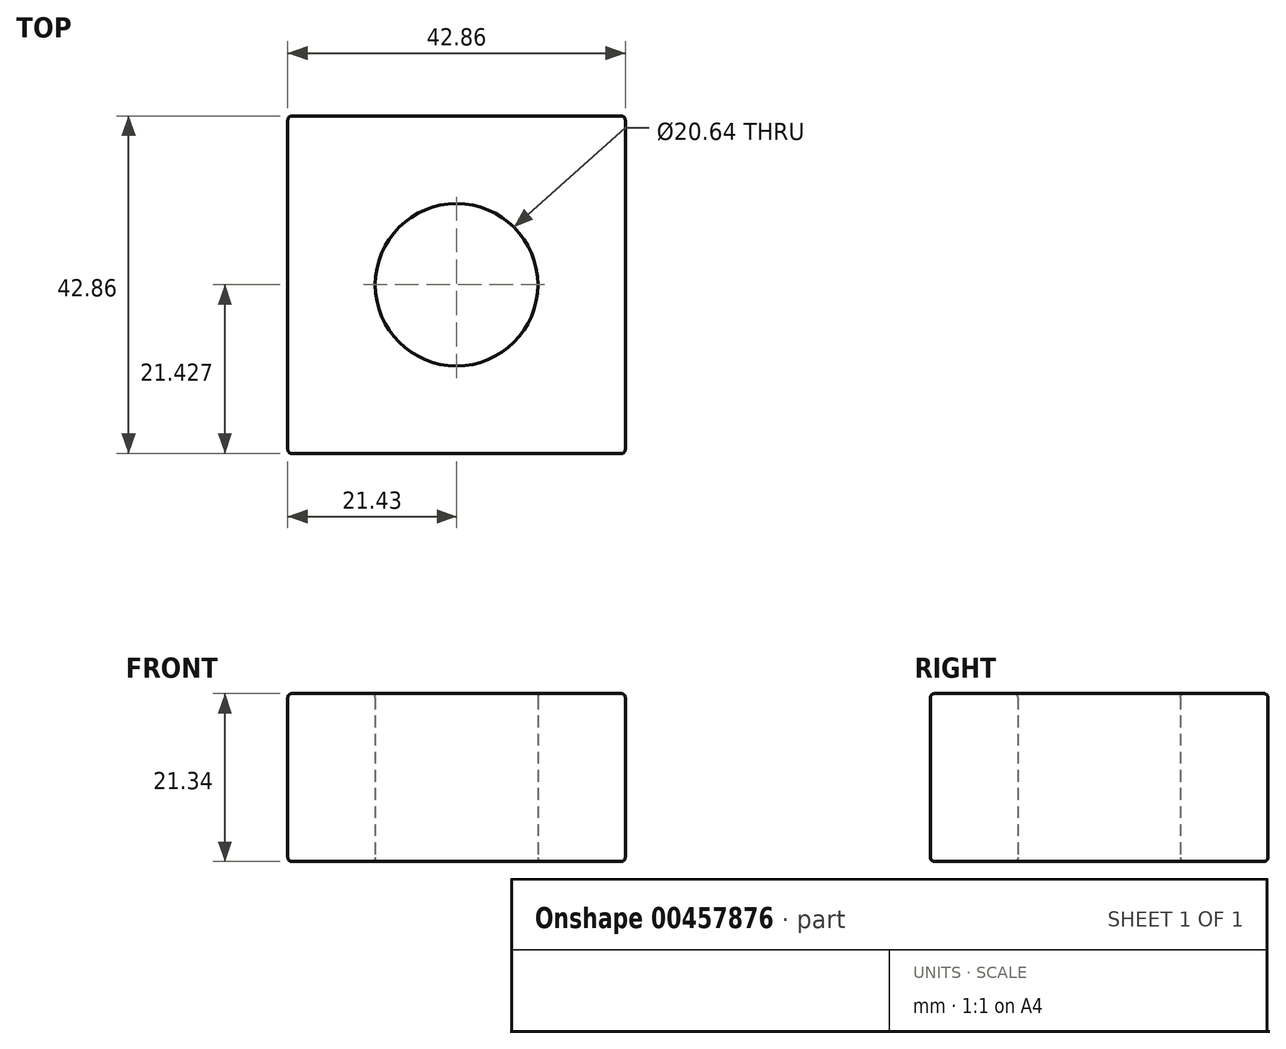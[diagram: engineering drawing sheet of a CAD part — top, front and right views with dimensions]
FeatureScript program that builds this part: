
annotation { "Feature Type Name" : "Feature", "Feature Type Description" : "" }
export const myFeature = defineFeature(function(context is Context, id is Id, definition is map)
    precondition{}
    {
        {
            var Q0;
            Q0=qCreatedBy(makeId("Top.planeOp"),FACE);
            var sketch = newSketch(context, id + "F0", { "sketchPlane" : qUnion([Q0])});
            skLineSegment(sketch, "E0.bottom", {"start": v(6.82, -5.16) * mm, "end": v(49.68, -5.16) * mm});
            skLineSegment(sketch, "E0.top", {"start": v(6.82, -48.02) * mm, "end": v(49.68, -48.02) * mm});
            skLineSegment(sketch, "E0.left", {"start": v(6.82, -5.16) * mm, "end": v(6.82, -48.02) * mm});
            skLineSegment(sketch, "E0.right", {"start": v(49.68, -5.16) * mm, "end": v(49.68, -48.02) * mm});
            skLineSegment(sketch, "E1", {"start": v(28.25, -5.16) * mm, "end": v(28.25, -48.02) * mm, "construction": true});
            skCircle(sketch, "E2", {"center": v(28.25, -26.6) * mm, "radius": 10.32 * mm});
            skSolve(sketch);
        }
        {
            var Q0;
            Q0 = qSketchRegion(id + "F0", true);
            extrude(context, id + "F1", {"entities" : qUnion([Q0]), "depth" : 21.34 * mm});
        }
        {
            var Q0;
            Q0=makeQuery(id+"F1.opExtrude","CAP_EDGE",EDGE,{"disambiguationData":[OSD([sQuery(id+"F0.wireOp",EDGE,"E0.bottom")])],"isStart":true});
            var Q1;
            Q1=makeQuery(id+"F1.opExtrude","SWEPT_EDGE",EDGE,{"disambiguationData":[OSD([sQuery(id+"F0.wireOp",EDGE,"E0.bottom"),sQuery(id+"F0.wireOp",EDGE,"E0.left")])]});
            var Q2;
            Q2=makeQuery(id+"F1.opExtrude","CAP_EDGE",EDGE,{"disambiguationData":[OSD([sQuery(id+"F0.wireOp",EDGE,"E0.bottom")])],"isStart":false});
            var Q3;
            Q3=makeQuery(id+"F1.opExtrude","SWEPT_FACE",FACE,{"disambiguationData":[OSD([sQuery(id+"F0.wireOp",EDGE,"E0.bottom")])]});
            var Q4;
            Q4=makeQuery(id+"F1.opExtrude","CAP_FACE",FACE,{"disambiguationData":[OSD([sQuery(id+"F0.wireOp",EDGE,"E0.bottom"),sQuery(id+"F0.wireOp",EDGE,"E0.top"),sQuery(id+"F0.wireOp",EDGE,"E0.left"),sQuery(id+"F0.wireOp",EDGE,"E0.right"),sQuery(id+"F0.wireOp",EDGE,"E2")])],"isStart":true});
            var Q5;
            Q5=makeQuery(id+"F1.opExtrude","SWEPT_FACE",FACE,{"disambiguationData":[OSD([sQuery(id+"F0.wireOp",EDGE,"E0.right")])]});
            var Q6;
            Q6=makeQuery(id+"F1.opExtrude","CAP_FACE",FACE,{"disambiguationData":[OSD([sQuery(id+"F0.wireOp",EDGE,"E0.bottom"),sQuery(id+"F0.wireOp",EDGE,"E0.top"),sQuery(id+"F0.wireOp",EDGE,"E0.left"),sQuery(id+"F0.wireOp",EDGE,"E0.right"),sQuery(id+"F0.wireOp",EDGE,"E2")])],"isStart":false});
            var Q7;
            Q7=makeQuery(id+"F1.opExtrude","SWEPT_EDGE",EDGE,{"disambiguationData":[OSD([sQuery(id+"F0.wireOp",EDGE,"E0.top"),sQuery(id+"F0.wireOp",EDGE,"E0.left")])]});
            fillet(context, id + "F2", {"entities" : qUnion([Q0, Q1, Q2, Q3, Q4, Q5, Q6, Q7]), "radius" : 0.5 * mm, "tangentPropagation" : true, "allowEdgeOverflow" : false});
        }
    });
